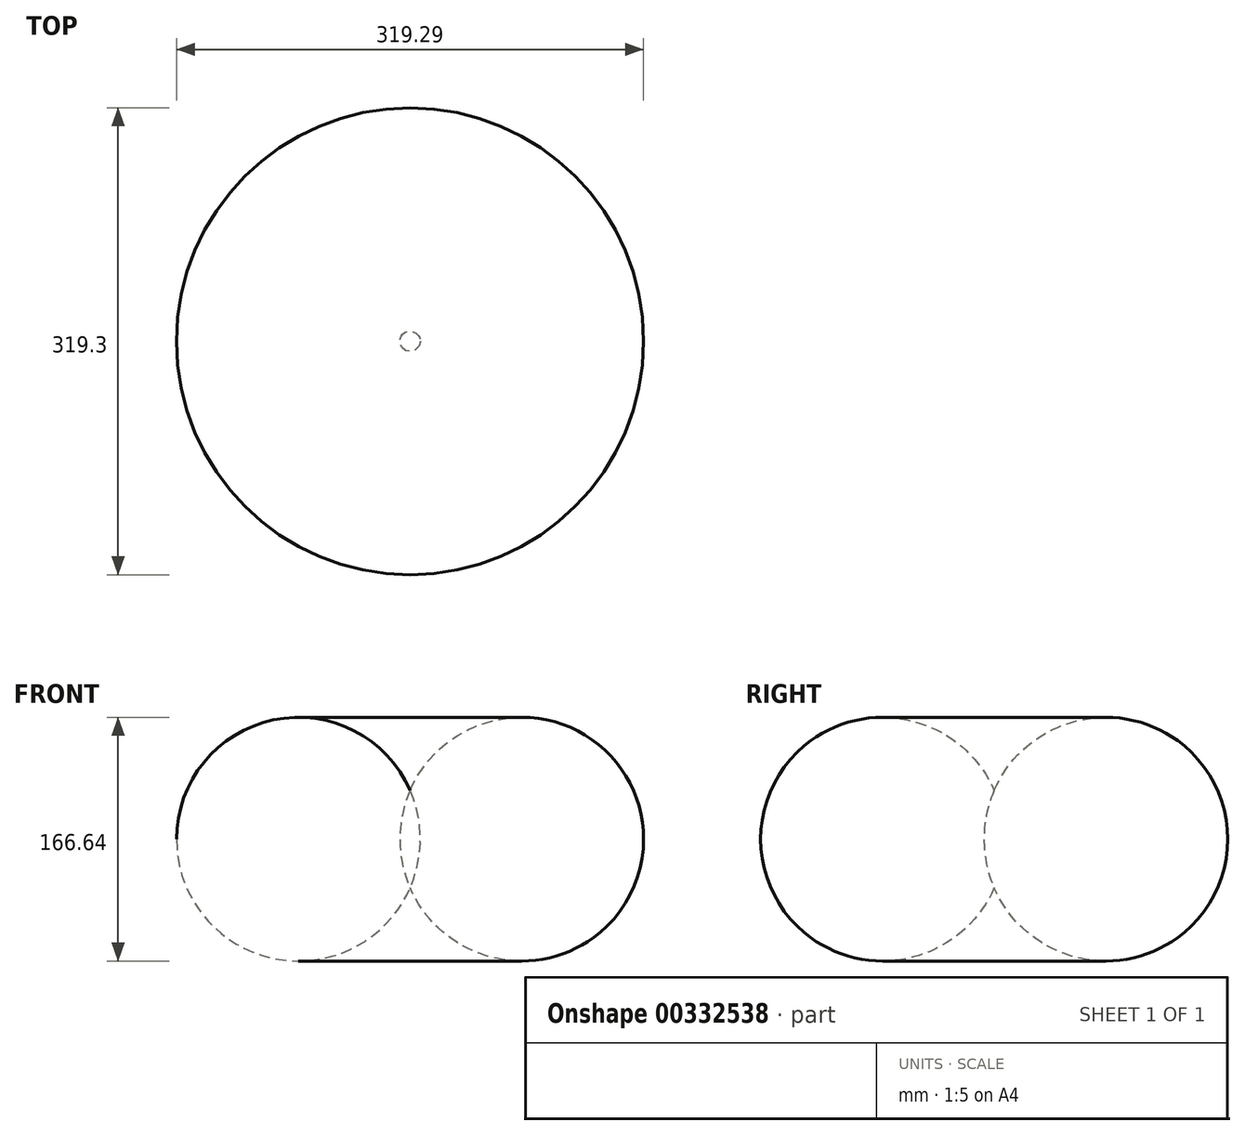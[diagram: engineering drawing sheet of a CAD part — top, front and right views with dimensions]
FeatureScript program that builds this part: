
annotation { "Feature Type Name" : "Feature", "Feature Type Description" : "" }
export const myFeature = defineFeature(function(context is Context, id is Id, definition is map)
    precondition{}
    {
        {
            var Q0;
            Q0=qCreatedBy(makeId("Front.planeOp"),FACE);
            var sketch = newSketch(context, id + "F0", { "sketchPlane" : qUnion([Q0])});
            skLineSegment(sketch, "E0", {"start": v(-76.33, -76.82) * mm, "end": v(-76.33, 75.2) * mm});
            skCircle(sketch, "E1", {"center": v(0, 0) * mm, "radius": 83.32 * mm});
            skSolve(sketch);
        }
        {
            var Q0;
            {var subQ0=sQuery(id+"F0.wireOp",EDGE,"E1");var subQ1=sQuery(id+"F0.wireOp",EDGE,"E0");var subQ2=makeQuery(id+"F0.imprint","INTERSECT",VERTEX,{"disambiguationData":[OD(0.0)],"derivedFrom":[subQ1,subQ0]});Q0=makeQuery(id+"F0.imprint","IMPRINT",FACE,{"disambiguationData":[TD([[makeQuery(id+"F0.imprint","IMPRINT",EDGE,{"disambiguationData":[TD([[subQ2,-1.0]])],"derivedFrom":subQ1}),-1.0]])]});}
            var Q1;
            Q1=sQuery(id+"F0.wireOp",EDGE,"E0");
            revolve(context, id + "F1", {"entities" : qUnion([Q0]), "axis" : qUnion([Q1]), "revolveType" : RevolveType.FULL});
        }
    });
